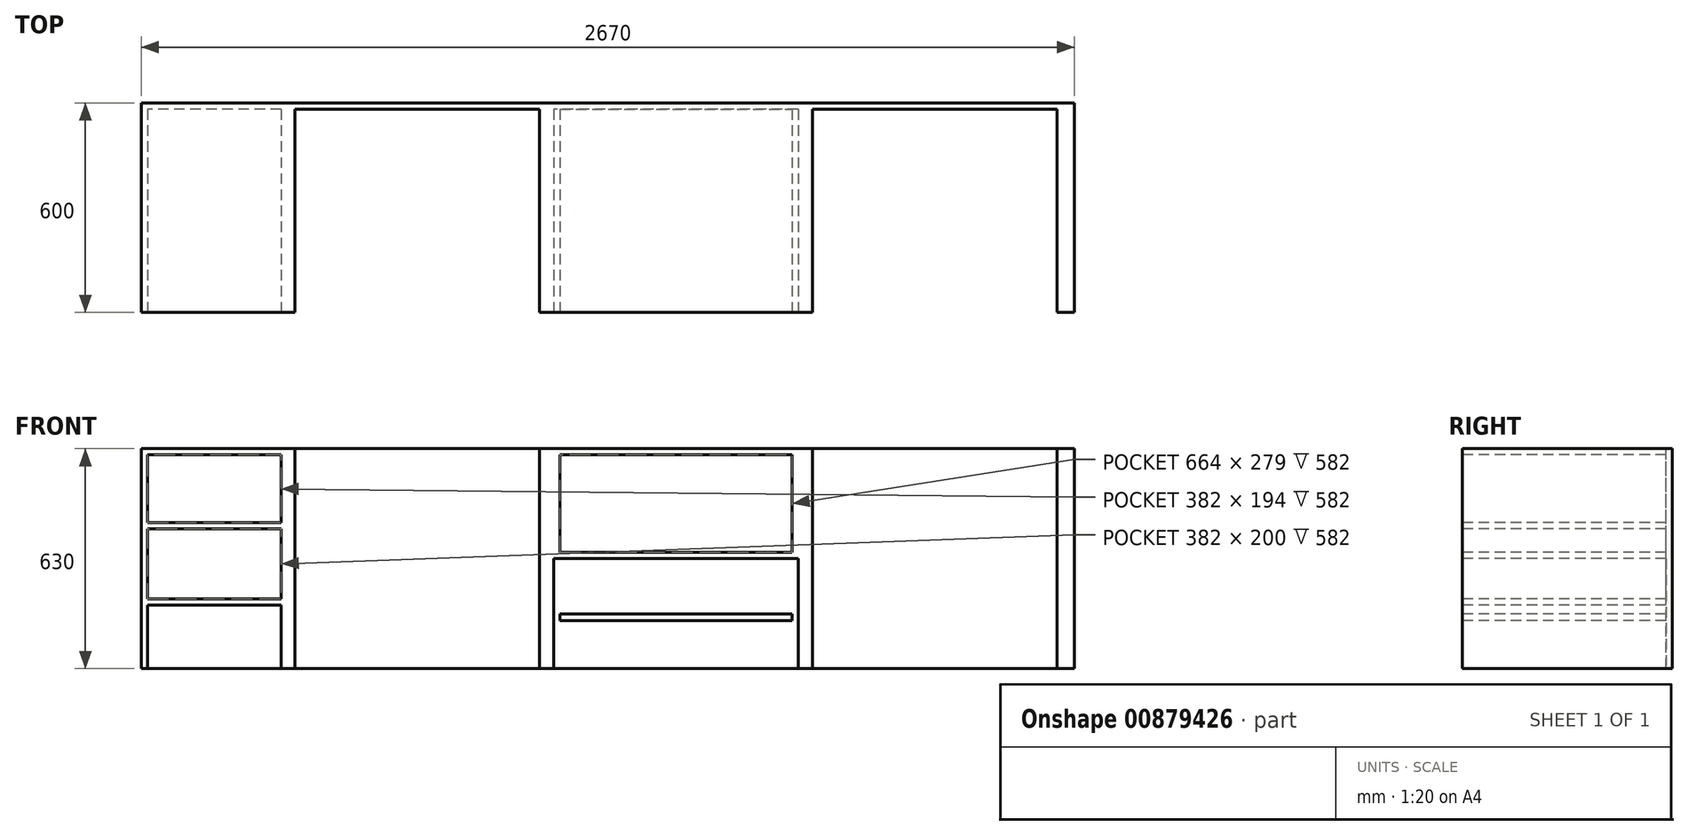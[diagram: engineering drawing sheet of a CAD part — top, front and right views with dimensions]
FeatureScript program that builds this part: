
annotation { "Feature Type Name" : "Feature", "Feature Type Description" : "" }
export const myFeature = defineFeature(function(context is Context, id is Id, definition is map)
    precondition{}
    {
        {
            var Q0;
            Q0=qCreatedBy(makeId("Front.planeOp"),FACE);
            var sketch = newSketch(context, id + "F0", { "sketchPlane" : qUnion([Q0])});
            skLineSegment(sketch, "E0.bottom", {"start": v(0, 0) * mm, "end": v(2670, 0) * mm});
            skLineSegment(sketch, "E0.top", {"start": v(0, 630) * mm, "end": v(1180, 630) * mm});
            skLineSegment(sketch, "E0.left", {"start": v(0, 0) * mm, "end": v(0, 630) * mm});
            skLineSegment(sketch, "E0.right", {"start": v(2670, 0) * mm, "end": v(2670, 630) * mm});
            skLineSegment(sketch, "E1.bottom", {"start": v(0, 0) * mm, "end": v(400, 0) * mm});
            skLineSegment(sketch, "E1.top", {"start": v(0, 630) * mm, "end": v(400, 630) * mm});
            skLineSegment(sketch, "E1.right", {"start": v(400, 0) * mm, "end": v(400, 612) * mm});
            skLineSegment(sketch, "E2.bottom", {"start": v(440, 0) * mm, "end": v(1140, 0) * mm});
            skLineSegment(sketch, "E2.top", {"start": v(440, 630) * mm, "end": v(1140, 630) * mm});
            skLineSegment(sketch, "E2.left", {"start": v(440, 0) * mm, "end": v(440, 630) * mm});
            skLineSegment(sketch, "E2.right", {"start": v(1180, 0) * mm, "end": v(1180, 315) * mm});
            skLineSegment(sketch, "E3.bottom", {"start": v(1180, 0) * mm, "end": v(1880, 0) * mm});
            skLineSegment(sketch, "E3.top", {"start": v(1180, 315) * mm, "end": v(1880, 315) * mm});
            skLineSegment(sketch, "E3.right", {"start": v(1920, 0) * mm, "end": v(1920, 315) * mm});
            skLineSegment(sketch, "E4.bottom", {"start": v(1880, 315) * mm, "end": v(1180, 315) * mm});
            skLineSegment(sketch, "E5.bottom", {"start": v(1920, 0) * mm, "end": v(2620, 0) * mm});
            skLineSegment(sketch, "E5.top", {"start": v(1920, 630) * mm, "end": v(2620, 630) * mm});
            skLineSegment(sketch, "E5.left", {"start": v(1920, 0) * mm, "end": v(1920, 630) * mm});
            skLineSegment(sketch, "E5.right", {"start": v(2620, 0) * mm, "end": v(2620, 630) * mm});
            skLineSegment(sketch, "E6", {"start": v(1140, 630) * mm, "end": v(1140, 0) * mm});
            skLineSegment(sketch, "E7.0", {"start": v(458, 18) * mm, "end": v(458, 612) * mm});
            skLineSegment(sketch, "E7.1", {"start": v(458, 18) * mm, "end": v(1122, 18) * mm});
            skLineSegment(sketch, "E7.2", {"start": v(1122, 612) * mm, "end": v(1122, 18) * mm});
            skLineSegment(sketch, "E7.3", {"start": v(458, 612) * mm, "end": v(1122, 612) * mm});
            skLineSegment(sketch, "E8", {"start": v(1180, 315) * mm, "end": v(1180, 630) * mm});
            skLineSegment(sketch, "E9", {"start": v(1880, 315) * mm, "end": v(1880, 0) * mm});
            skLineSegment(sketch, "E10", {"start": v(1880, 315) * mm, "end": v(1880, 630) * mm});
            skLineSegment(sketch, "E11", {"start": v(1180, 630) * mm, "end": v(1880, 630) * mm});
            skLineSegment(sketch, "E12", {"start": v(1880, 630) * mm, "end": v(1880, 630) * mm});
            skLineSegment(sketch, "E13", {"start": v(1880, 630) * mm, "end": v(2670, 630) * mm});
            skLineSegment(sketch, "E14.0", {"start": v(1198, 612) * mm, "end": v(1862, 612) * mm});
            skLineSegment(sketch, "E14.1", {"start": v(1198, 333) * mm, "end": v(1198, 612) * mm});
            skLineSegment(sketch, "E14.2", {"start": v(1198, 333) * mm, "end": v(1862, 333) * mm});
            skLineSegment(sketch, "E14.3", {"start": v(1862, 333) * mm, "end": v(1862, 612) * mm});
            skLineSegment(sketch, "E15.0", {"start": v(1862, 297) * mm, "end": v(1862, 18) * mm});
            skLineSegment(sketch, "E15.1", {"start": v(1198, 297) * mm, "end": v(1862, 297) * mm});
            skLineSegment(sketch, "E15.2", {"start": v(1198, 18) * mm, "end": v(1198, 297) * mm});
            skLineSegment(sketch, "E15.3", {"start": v(1198, 18) * mm, "end": v(1862, 18) * mm});
            skLineSegment(sketch, "E16.0", {"start": v(1938, 18) * mm, "end": v(1938, 612) * mm});
            skLineSegment(sketch, "E16.1", {"start": v(1938, 18) * mm, "end": v(2602, 18) * mm});
            skLineSegment(sketch, "E16.2", {"start": v(2602, 18) * mm, "end": v(2602, 612) * mm});
            skLineSegment(sketch, "E16.3", {"start": v(1938, 612) * mm, "end": v(2602, 612) * mm});
            skLineSegment(sketch, "E17", {"start": v(18, 200) * mm, "end": v(400, 200) * mm});
            skLineSegment(sketch, "E18", {"start": v(18, 182) * mm, "end": v(400, 182) * mm});
            skLineSegment(sketch, "E19", {"start": v(18, 418) * mm, "end": v(400, 418) * mm});
            skLineSegment(sketch, "E20", {"start": v(18, 400) * mm, "end": v(400, 400) * mm});
            skLineSegment(sketch, "E21", {"start": v(18, 612) * mm, "end": v(18, 0) * mm});
            skLineSegment(sketch, "E22", {"start": v(400, 18) * mm, "end": v(18, 18) * mm});
            skLineSegment(sketch, "E23", {"start": v(400, 612) * mm, "end": v(18, 612) * mm});
            skLineSegment(sketch, "E24.bottom", {"start": v(1198, 138) * mm, "end": v(1862, 138) * mm});
            skLineSegment(sketch, "E24.top", {"start": v(1198, 156) * mm, "end": v(1862, 156) * mm});
            skLineSegment(sketch, "E24.left", {"start": v(1198, 138) * mm, "end": v(1198, 156) * mm});
            skLineSegment(sketch, "E24.right", {"start": v(1862, 138) * mm, "end": v(1862, 156) * mm});
            skSolve(sketch);
        }
        {
            var Q0;
            Q0=makeQuery(id+"F0.imprint","IMPRINT",FACE,{"disambiguationData":[TD([[makeQuery(id+"F0.imprint","IMPRINT",EDGE,{"derivedFrom":sQuery(id+"F0.wireOp",EDGE,"E1.bottom")}),1.0]])]});
            var Q1;
            {var subQ0=sQuery(id+"F0.wireOp",EDGE,"E1.right");Q1=makeQuery(id+"F0.imprint","IMPRINT",FACE,{"disambiguationData":[TD([[makeQuery(id+"F0.imprint","IMPRINT",EDGE,{"derivedFrom":subQ0}),-1.0]])]});}
            var Q2;
            Q2=makeQuery(id+"F0.imprint","IMPRINT",FACE,{"disambiguationData":[TD([[makeQuery(id+"F0.imprint","IMPRINT",EDGE,{"derivedFrom":sQuery(id+"F0.wireOp",EDGE,"E2.bottom")}),1.0]])]});
            var Q3;
            {var subQ6=sQuery(id+"F0.wireOp",EDGE,"E6");Q3=makeQuery(id+"F0.imprint","IMPRINT",FACE,{"disambiguationData":[TD([[makeQuery(id+"F0.imprint","IMPRINT",EDGE,{"derivedFrom":subQ6}),1.0]])]});}
            var Q4;
            {var subQ2=sQuery(id+"F0.wireOp",EDGE,"E3.top");Q4=makeQuery(id+"F0.imprint","IMPRINT",FACE,{"disambiguationData":[TD([[makeQuery(id+"F0.imprint","IMPRINT",EDGE,{"derivedFrom":subQ2}),1.0]])]});}
            var Q5;
            {var subQ1=sQuery(id+"F0.wireOp",EDGE,"E3.bottom");Q5=makeQuery(id+"F0.imprint","IMPRINT",FACE,{"disambiguationData":[TD([[makeQuery(id+"F0.imprint","IMPRINT",EDGE,{"derivedFrom":subQ1}),1.0]])]});}
            var Q6;
            {var subQ0=sQuery(id+"F0.wireOp",EDGE,"E5.left");Q6=makeQuery(id+"F0.imprint","IMPRINT",FACE,{"disambiguationData":[TD([[makeQuery(id+"F0.imprint","IMPRINT",EDGE,{"derivedFrom":subQ0}),1.0]])]});}
            var Q7;
            Q7=makeQuery(id+"F0.imprint","IMPRINT",FACE,{"disambiguationData":[TD([[makeQuery(id+"F0.imprint","IMPRINT",EDGE,{"derivedFrom":sQuery(id+"F0.wireOp",EDGE,"E5.bottom")}),1.0]])]});
            var Q8;
            {var subQ0=sQuery(id+"F0.wireOp",EDGE,"E0.right");Q8=makeQuery(id+"F0.imprint","IMPRINT",FACE,{"disambiguationData":[TD([[makeQuery(id+"F0.imprint","IMPRINT",EDGE,{"derivedFrom":subQ0}),1.0]])]});}
            var Q9;
            {var subQ0=sQuery(id+"F0.wireOp",EDGE,"E1.top");Q9=makeQuery(id+"F0.imprint","IMPRINT",FACE,{"disambiguationData":[TD([[makeQuery(id+"F0.imprint","IMPRINT",EDGE,{"derivedFrom":subQ0}),-1.0]])]});}
            var Q10;
            {var subQ0=sQuery(id+"F0.wireOp",EDGE,"E17");Q10=makeQuery(id+"F0.imprint","IMPRINT",FACE,{"disambiguationData":[TD([[makeQuery(id+"F0.imprint","IMPRINT",EDGE,{"derivedFrom":subQ0}),-1.0]])]});}
            var Q11;
            {var subQ0=sQuery(id+"F0.wireOp",EDGE,"E19");Q11=makeQuery(id+"F0.imprint","IMPRINT",FACE,{"disambiguationData":[TD([[makeQuery(id+"F0.imprint","IMPRINT",EDGE,{"derivedFrom":subQ0}),-1.0]])]});}
            var Q12;
            Q12=makeQuery(id+"F0.imprint","IMPRINT",FACE,{"disambiguationData":[TD([[makeQuery(id+"F0.imprint","IMPRINT",EDGE,{"derivedFrom":sQuery(id+"F0.wireOp",EDGE,"E4.bottom")}),-1.0]])]});
            var Q13;
            Q13=makeQuery(id+"F0.imprint","IMPRINT",FACE,{"disambiguationData":[TD([[makeQuery(id+"F0.imprint","IMPRINT",EDGE,{"derivedFrom":sQuery(id+"F0.wireOp",EDGE,"E24.bottom")}),1.0]])]});
            extrude(context, id + "F1", {"entities" : qUnion([Q0, Q1, Q2, Q3, Q4, Q5, Q6, Q7, Q8, Q9, Q10, Q11, Q12, Q13]), "oppositeDirection" : true, "depth" : 600 * mm, "offsetDistance" : 25 * mm});
        }
        {
            var Q0;
            Q0=makeQuery(id+"F1.opExtrude","CAP_FACE",FACE,{"disambiguationData":[OSD([sQuery(id+"F0.wireOp",EDGE,"E0.bottom"),sQuery(id+"F0.wireOp",EDGE,"E0.top"),sQuery(id+"F0.wireOp",EDGE,"E0.right"),sQuery(id+"F0.wireOp",EDGE,"E1.bottom"),sQuery(id+"F0.wireOp",EDGE,"E1.top"),sQuery(id+"F0.wireOp",EDGE,"E0.left"),sQuery(id+"F0.wireOp",EDGE,"E1.right"),sQuery(id+"F0.wireOp",EDGE,"E2.bottom"),sQuery(id+"F0.wireOp",EDGE,"E2.top"),sQuery(id+"F0.wireOp",EDGE,"E3.bottom"),sQuery(id+"F0.wireOp",EDGE,"E5.bottom"),sQuery(id+"F0.wireOp",EDGE,"E7.0"),sQuery(id+"F0.wireOp",EDGE,"E7.1"),sQuery(id+"F0.wireOp",EDGE,"E7.2"),sQuery(id+"F0.wireOp",EDGE,"E7.3"),sQuery(id+"F0.wireOp",EDGE,"E11"),sQuery(id+"F0.wireOp",EDGE,"E13"),sQuery(id+"F0.wireOp",EDGE,"E14.0"),sQuery(id+"F0.wireOp",EDGE,"E14.1"),sQuery(id+"F0.wireOp",EDGE,"E14.2"),sQuery(id+"F0.wireOp",EDGE,"E14.3"),sQuery(id+"F0.wireOp",EDGE,"E15.0"),sQuery(id+"F0.wireOp",EDGE,"E15.1"),sQuery(id+"F0.wireOp",EDGE,"E15.2"),sQuery(id+"F0.wireOp",EDGE,"E15.3"),sQuery(id+"F0.wireOp",EDGE,"E16.0"),sQuery(id+"F0.wireOp",EDGE,"E16.1"),sQuery(id+"F0.wireOp",EDGE,"E16.2"),sQuery(id+"F0.wireOp",EDGE,"E16.3"),sQuery(id+"F0.wireOp",EDGE,"E17"),sQuery(id+"F0.wireOp",EDGE,"E18"),sQuery(id+"F0.wireOp",EDGE,"E19"),sQuery(id+"F0.wireOp",EDGE,"E20"),sQuery(id+"F0.wireOp",EDGE,"E21"),sQuery(id+"F0.wireOp",EDGE,"E22"),sQuery(id+"F0.wireOp",EDGE,"E23")])],"isStart":false});
            var sketch = newSketch(context, id + "F2", { "sketchPlane" : qUnion([Q0])});
            skLineSegment(sketch, "E25.bottom", {"start": v(-2670, 630) * mm, "end": v(0, 630) * mm});
            skLineSegment(sketch, "E25.top", {"start": v(-2670, 0) * mm, "end": v(0, 0) * mm});
            skLineSegment(sketch, "E25.left", {"start": v(-2670, 630) * mm, "end": v(-2670, 0) * mm});
            skLineSegment(sketch, "E25.right", {"start": v(0, 630) * mm, "end": v(0, 0) * mm});
            skSolve(sketch);
        }
        {
            var Q0;
            Q0 = qSketchRegion(id + "F2", true);
            extrude(context, id + "F3", {"entities" : qUnion([Q0]), "operationType" : NewBodyOperationType.ADD, "surfaceOperationType" : NewSurfaceOperationType.ADD, "oppositeDirection" : true, "depth" : 18 * mm, "offsetDistance" : 25 * mm});
        }
    });
